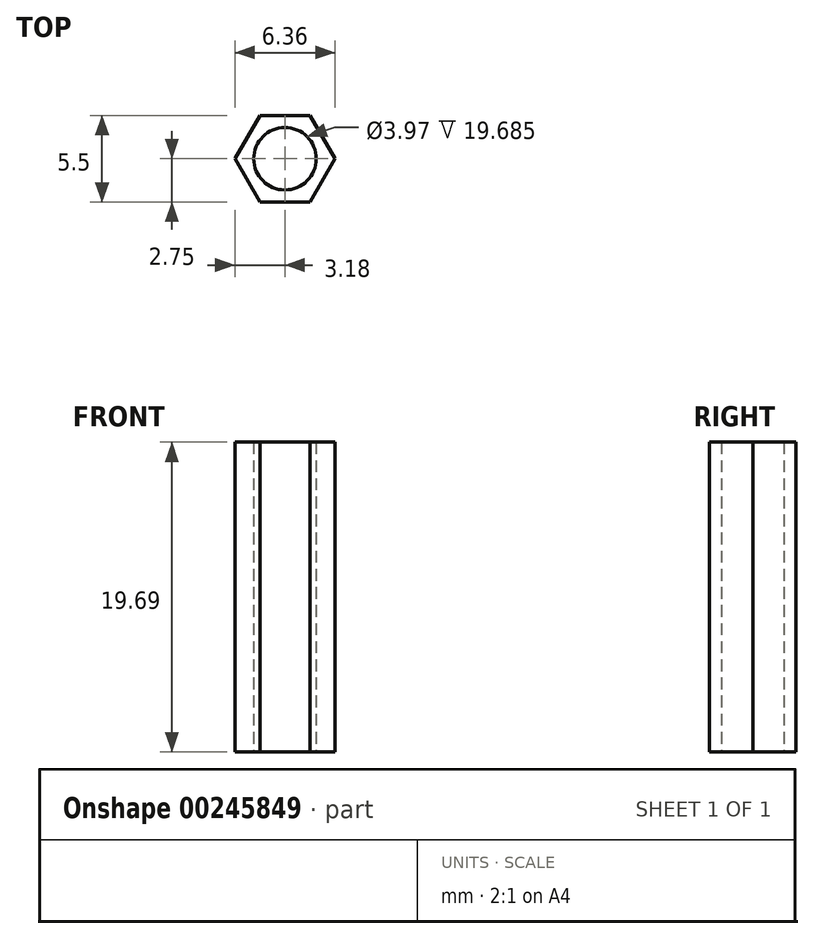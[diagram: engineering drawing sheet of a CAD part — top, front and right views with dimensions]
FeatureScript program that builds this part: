
annotation { "Feature Type Name" : "Feature", "Feature Type Description" : "" }
export const myFeature = defineFeature(function(context is Context, id is Id, definition is map)
    precondition{}
    {
        {
            var Q0;
            Q0=qCreatedBy(makeId("Top.planeOp"),FACE);
            var sketch = newSketch(context, id + "F0", { "sketchPlane" : qUnion([Q0])});
            skCircle(sketch, "E0.cCircle", {"center": v(0, 0) * mm, "radius": 2.75 * mm, "construction": true});
            skLineSegment(sketch, "E0.0", {"start": v(-1.59, 2.75) * mm, "end": v(1.59, 2.75) * mm});
            skLineSegment(sketch, "E0.1", {"start": v(1.59, 2.75) * mm, "end": v(3.18, 0) * mm});
            skLineSegment(sketch, "E0.2", {"start": v(3.18, 0) * mm, "end": v(1.59, -2.75) * mm});
            skLineSegment(sketch, "E0.3", {"start": v(1.59, -2.75) * mm, "end": v(-1.59, -2.75) * mm});
            skLineSegment(sketch, "E0.4", {"start": v(-1.59, -2.75) * mm, "end": v(-3.18, 0) * mm});
            skLineSegment(sketch, "E0.5", {"start": v(-3.18, 0) * mm, "end": v(-1.59, 2.75) * mm});
            skPoint(sketch, "E0.0.midPoint", {"position": v(0, 2.75) * mm});
            skCircle(sketch, "E1", {"center": v(0, 0) * mm, "radius": 1.98 * mm});
            skSolve(sketch);
        }
        {
            var Q0;
            Q0=makeQuery(id+"F0.imprint","IMPRINT",FACE,{"disambiguationData":[TD([[makeQuery(id+"F0.imprint","IMPRINT",EDGE,{"derivedFrom":sQuery(id+"F0.wireOp",EDGE,"E0.0")}),-1.0]])]});
            extrude(context, id + "F1", {"entities" : qUnion([Q0]), "depth" : 19.68 * mm});
        }
    });
